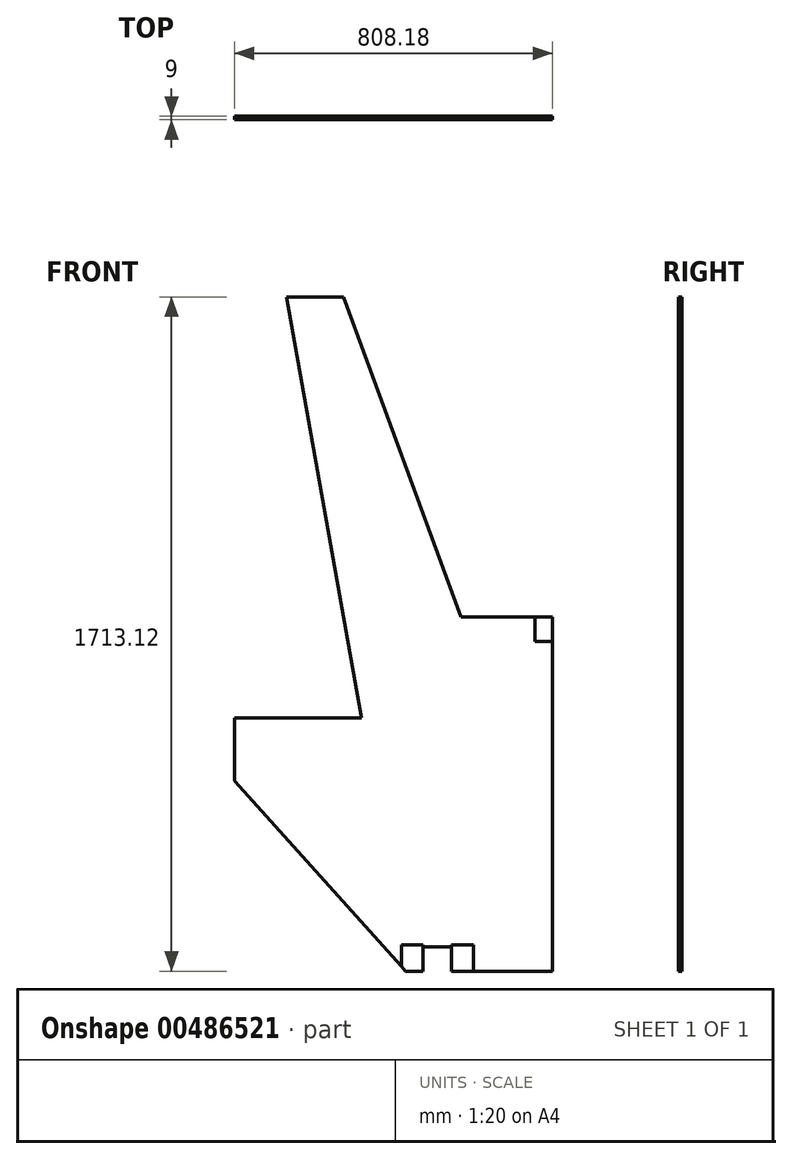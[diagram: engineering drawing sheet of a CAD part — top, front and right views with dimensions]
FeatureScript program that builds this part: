
annotation { "Feature Type Name" : "Feature", "Feature Type Description" : "" }
export const myFeature = defineFeature(function(context is Context, id is Id, definition is map)
    precondition{}
    {
        {
            var Q0;
            Q0=qCreatedBy(makeId("Front.planeOp"),FACE);
            var sketch = newSketch(context, id + "F0", { "sketchPlane" : qUnion([Q0])});
            skLineSegment(sketch, "E0", {"start": v(-373.95, 0) * mm, "end": v(-808.5, 483.39) * mm});
            skLineSegment(sketch, "E1", {"start": v(-808.5, 483.39) * mm, "end": v(-808.5, 643.39) * mm});
            skLineSegment(sketch, "E2", {"start": v(-808.5, 643.39) * mm, "end": v(-486.5, 643.39) * mm});
            skLineSegment(sketch, "E3", {"start": v(-486.5, 643.39) * mm, "end": v(-676.3, 1713.12) * mm});
            skLineSegment(sketch, "E4", {"start": v(-676.3, 1713.12) * mm, "end": v(-531.3, 1713.12) * mm});
            skLineSegment(sketch, "E5", {"start": v(-531.3, 1713.12) * mm, "end": v(-233.32, 900) * mm});
            skLineSegment(sketch, "E6", {"start": v(-233.32, 900) * mm, "end": v(-0.32, 900) * mm});
            skLineSegment(sketch, "E7", {"start": v(-0.32, 900) * mm, "end": v(-0.32, 0) * mm});
            skLineSegment(sketch, "E8", {"start": v(-373.95, 0) * mm, "end": v(-329.95, 0) * mm});
            skLineSegment(sketch, "E9", {"start": v(-45.32, 900) * mm, "end": v(-45.32, 838) * mm});
            skLineSegment(sketch, "E10", {"start": v(-45.32, 838) * mm, "end": v(-0.32, 838) * mm});
            skLineSegment(sketch, "E11", {"start": v(-329.95, 0) * mm, "end": v(-329.95, 62) * mm});
            skLineSegment(sketch, "E12", {"start": v(-329.95, 62) * mm, "end": v(-256.95, 62) * mm});
            skLineSegment(sketch, "E13", {"start": v(-256.95, 62) * mm, "end": v(-256.95, 0) * mm});
            skLineSegment(sketch, "E14.trimOffspring", {"start": v(-256.95, 0) * mm, "end": v(-0.32, 0) * mm});
            skLineSegment(sketch, "E15", {"start": v(-329.95, 67) * mm, "end": v(-329.95, 62) * mm});
            skLineSegment(sketch, "E16", {"start": v(-329.95, 67) * mm, "end": v(-384.95, 67) * mm});
            skLineSegment(sketch, "E17", {"start": v(-384.95, 67) * mm, "end": v(-384.95, 12.24) * mm});
            skLineSegment(sketch, "E18", {"start": v(-256.95, 67) * mm, "end": v(-256.95, 62) * mm});
            skLineSegment(sketch, "E19", {"start": v(-256.95, 67) * mm, "end": v(-201.95, 67) * mm});
            skLineSegment(sketch, "E20", {"start": v(-201.95, 67) * mm, "end": v(-201.95, 0) * mm});
            skSolve(sketch);
        }
        {
            var Q0;
            {var subQ7=sQuery(id+"F0.wireOp",EDGE,"E1");Q0=makeQuery(id+"F0.imprint","IMPRINT",FACE,{"disambiguationData":[TD([[makeQuery(id+"F0.imprint","IMPRINT",EDGE,{"derivedFrom":subQ7}),-1.0]])]});}
            var Q1;
            {var subQ0=sQuery(id+"F0.wireOp",EDGE,"E8");Q1=makeQuery(id+"F0.imprint","IMPRINT",FACE,{"disambiguationData":[TD([[makeQuery(id+"F0.imprint","IMPRINT",EDGE,{"derivedFrom":subQ0}),1.0]])]});}
            var Q2;
            {var subQ1=sQuery(id+"F0.wireOp",EDGE,"E13");Q2=makeQuery(id+"F0.imprint","IMPRINT",FACE,{"disambiguationData":[TD([[makeQuery(id+"F0.imprint","IMPRINT",EDGE,{"derivedFrom":subQ1}),1.0]])]});}
            var Q3;
            {var subQ3=sQuery(id+"F0.wireOp",EDGE,"E9");Q3=makeQuery(id+"F0.imprint","IMPRINT",FACE,{"disambiguationData":[TD([[makeQuery(id+"F0.imprint","IMPRINT",EDGE,{"derivedFrom":subQ3}),1.0]])]});}
            extrude(context, id + "F1", {"entities" : qUnion([Q0, Q1, Q2, Q3]), "oppositeDirection" : true, "depth" : 9 * mm, "offsetDistance" : 25 * mm});
        }
        {
            var Q0;
            {var subQ3=sQuery(id+"F0.wireOp",EDGE,"E9");Q0=makeQuery(id+"F0.imprint","IMPRINT",FACE,{"disambiguationData":[TD([[makeQuery(id+"F0.imprint","IMPRINT",EDGE,{"derivedFrom":subQ3}),1.0]])]});}
            var Q1;
            {var subQ0=sQuery(id+"F0.wireOp",EDGE,"E8");Q1=makeQuery(id+"F0.imprint","IMPRINT",FACE,{"disambiguationData":[TD([[makeQuery(id+"F0.imprint","IMPRINT",EDGE,{"derivedFrom":subQ0}),1.0]])]});}
            var Q2;
            {var subQ1=sQuery(id+"F0.wireOp",EDGE,"E13");Q2=makeQuery(id+"F0.imprint","IMPRINT",FACE,{"disambiguationData":[TD([[makeQuery(id+"F0.imprint","IMPRINT",EDGE,{"derivedFrom":subQ1}),1.0]])]});}
            extrude(context, id + "F2", {"entities" : qUnion([Q0, Q1, Q2]), "operationType" : NewBodyOperationType.REMOVE, "oppositeDirection" : true, "depth" : 5 * mm, "offsetDistance" : 25 * mm});
        }
    });
